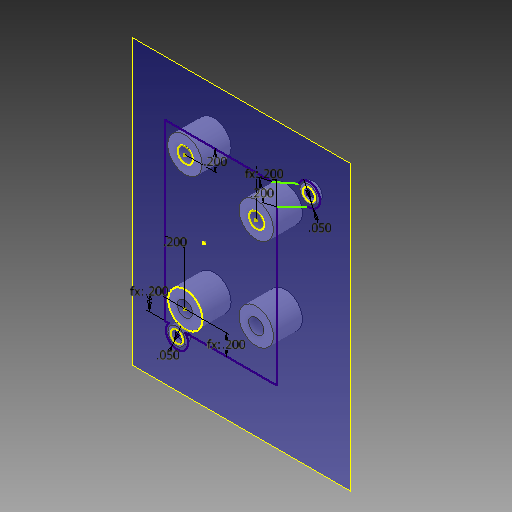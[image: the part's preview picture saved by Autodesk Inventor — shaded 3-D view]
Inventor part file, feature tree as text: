
AUTODESK INVENTOR PART (.ipt)
format: ipt  version: 2017 (Build 210142000, 142)  size: 157,696 bytes
history: native  units: in
note: dims shown in document units (in); Inventor stores cm internally (conversion verified against a paired STEP export)
features: reference x8, other x4, sketch x3, plane x3, extrude x2
ambient origin geometry x8: Origin, YZ Plane, XZ Plane, XY Plane, X Axis, Y Axis, Z Axis, Center Point
bodies: Solid1 (feature_tree)
feature tree (20):
  sketch  "Sketch1"  dims[d0=1.0in d1=0.0in d2=0.05in d3=0.0in]
  plane  "Work Plane1"
  extrude  "Extrusion1"  Depth=0.05in TaperAngle=0.0deg
  plane  "Work Plane2"
  extrude  "Extrusion2"  Depth=0.05in
  plane  "Work Plane3"
  sketch  "Sketch4"  dims[d6=0.2in d7=0.2in d8=0.2in d9=0.2in d10=0.05in d11=0.2in]
  reference  "Reference1"
  reference  "Reference2"
  reference  "Reference3"
  reference  "Reference4"
  reference  "Reference5"
  sketch  "Sketch3"  dims[d4=0.05in d5=0.2in]
  reference  "Reference6"
  reference  "Reference7"
  reference  "Reference8"
  other  "<userpath>\Documents\Inventor\PixyCam and Gimbal\Assembly2.iam"
  other  "Assembly2.iam"
  other  "Ring Holder:1"
  other  "frontCase:1"
